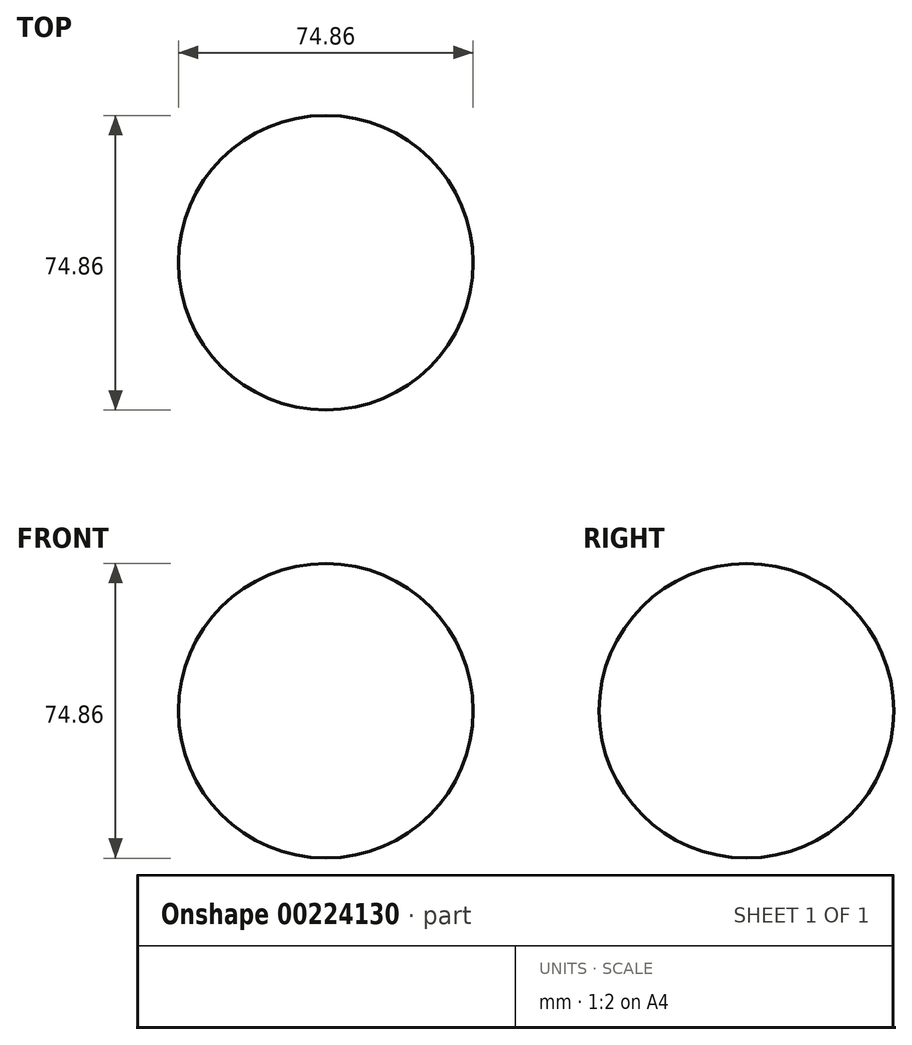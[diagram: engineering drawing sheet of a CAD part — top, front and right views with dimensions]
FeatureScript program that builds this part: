
annotation { "Feature Type Name" : "Feature", "Feature Type Description" : "" }
export const myFeature = defineFeature(function(context is Context, id is Id, definition is map)
    precondition{}
    {
        {
            var Q0;
            Q0=qCreatedBy(makeId("Front.planeOp"),FACE);
            var sketch = newSketch(context, id + "F0", { "sketchPlane" : qUnion([Q0])});
            skCircle(sketch, "E0", {"center": v(0, 0) * mm, "radius": 37.43 * mm});
            skLineSegment(sketch, "E1", {"start": v(0, 37.43) * mm, "end": v(0, -37.43) * mm});
            skSolve(sketch);
        }
        {
            var Q0;
            {var subQ0=sQuery(id+"F0.wireOp",EDGE,"E1");Q0=makeQuery(id+"F0.imprint","IMPRINT",FACE,{"disambiguationData":[TD([[makeQuery(id+"F0.imprint","IMPRINT",EDGE,{"derivedFrom":subQ0}),1.0]])]});}
            var Q1;
            Q1=sQuery(id+"F0.wireOp",EDGE,"E1");
            revolve(context, id + "F1", {"entities" : qUnion([Q0]), "axis" : qUnion([Q1]), "revolveType" : RevolveType.FULL});
        }
    });
